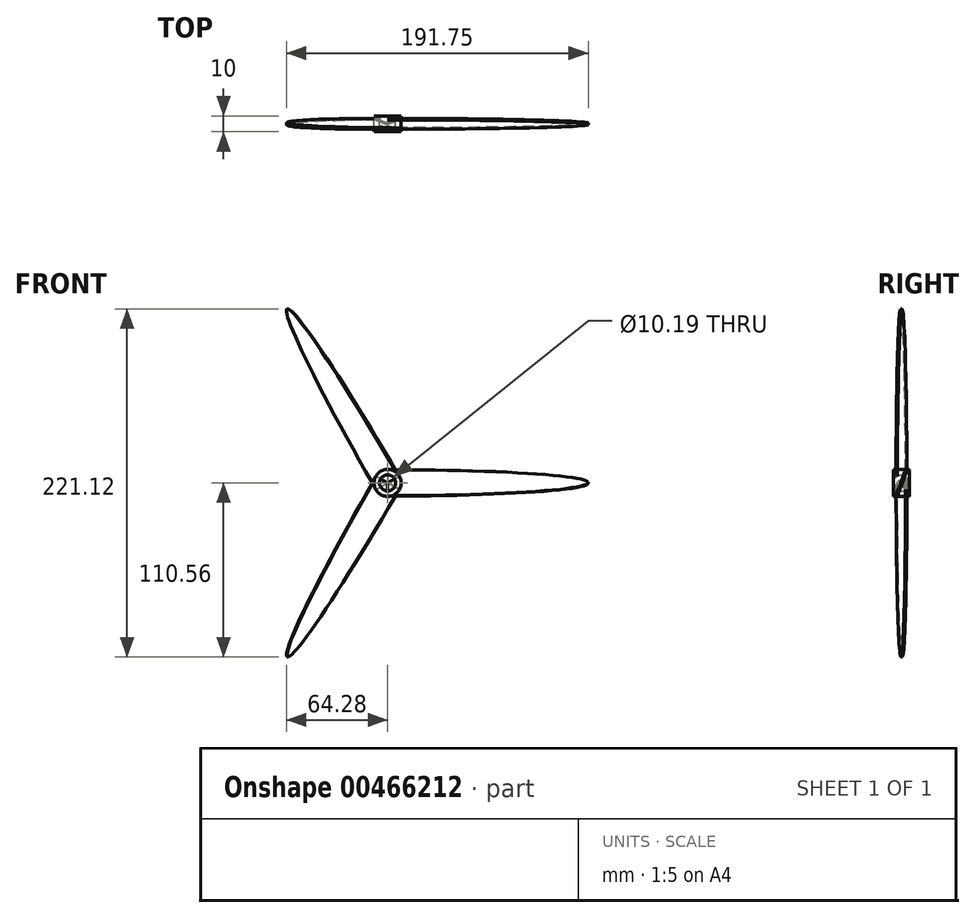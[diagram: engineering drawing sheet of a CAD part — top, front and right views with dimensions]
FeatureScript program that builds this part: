
annotation { "Feature Type Name" : "Feature", "Feature Type Description" : "" }
export const myFeature = defineFeature(function(context is Context, id is Id, definition is map)
    precondition{}
    {
        {
            var Q0;
            Q0=qCreatedBy(makeId("Front.planeOp"),FACE);
            var sketch = newSketch(context, id + "F0", { "sketchPlane" : qUnion([Q0])});
            skCircle(sketch, "E0", {"center": v(0, 0) * mm, "radius": 8.63 * mm});
            skCircle(sketch, "E1", {"center": v(0, 0) * mm, "radius": 5.1 * mm});
            skSolve(sketch);
        }
        {
            var Q0;
            Q0=qCreatedBy(makeId("Right.planeOp"),FACE);
            var sketch = newSketch(context, id + "F1", { "sketchPlane" : qUnion([Q0])});
            skLineSegment(sketch, "E2", {"start": v(23.78, 65.34) * mm, "end": v(-10.7, -29.37) * mm, "construction": true});
            skSolve(sketch);
        }
        {
            var Q0;
            Q0=qCreatedBy(makeId("Front.planeOp"),FACE);
            var Q1;
            Q1=sQuery(id+"F1.wireOp",EDGE,"E2");
            cPlane(context, id + "F2", {"entities" : qUnion([Q0, Q1]), "cplaneType" : CPlaneType.LINE_ANGLE, "offset" : 25 * mm, "angle" : 0 * degree, "width" : 150 * mm, "height" : 150 * mm});
        }
        {
            var Q0;
            Q0=qCreatedBy(id+"F2.planeOp",FACE);
            var sketch = newSketch(context, id + "F3", { "sketchPlane" : qUnion([Q0])});
            skEllipse(sketch, "E3", {"center": v(0, 0) * mm, "majorRadius": 127.47 * mm, "minorRadius": 8.77 * mm, "majorAxis": v(-1, 0)});
            skLineSegment(sketch, "E4", {"start": v(0, 8.77) * mm, "end": v(0, -8.77) * mm});
            skSolve(sketch);
        }
        {
            var Q0;
            {var subQ0=sQuery(id+"F3.wireOp",EDGE,"E4");Q0=makeQuery(id+"F3.imprint","IMPRINT",FACE,{"disambiguationData":[TD([[makeQuery(id+"F3.imprint","IMPRINT",EDGE,{"derivedFrom":subQ0}),-1.0]])]});}
            extrude(context, id + "F4", {"entities" : qUnion([Q0]), "endBound" : BoundingType.SYMMETRIC, "depth" : 1 * mm});
        }
        {
            var Q0;
            Q0=qCreatedBy(makeId("Top.planeOp"),FACE);
            var sketch = newSketch(context, id + "F5", { "sketchPlane" : qUnion([Q0])});
            skLineSegment(sketch, "E5", {"start": v(0, 41) * mm, "end": v(0, -39.52) * mm, "construction": true});
            skSolve(sketch);
        }
        {
            var Q0;
            Q0=makeQuery(id+"F4.opExtrude","SWEPT_BODY",BODY,{"disambiguationData":[OSD([sQuery(id+"F3.wireOp",EDGE,"E3"),sQuery(id+"F3.wireOp",EDGE,"E4")])]});
            var Q1;
            Q1=sQuery(id+"F5.wireOp",EDGE,"E5");
            circularPattern(context, id + "F6", {"entities" : qUnion([Q0]), "axis" : qUnion([Q1]), "angle" : 360 * degree, "instanceCount" : 3, "equalSpace" : true});
        }
        {
            var Q0;
            Q0=makeQuery(id+"F0.imprint","IMPRINT",FACE,{"disambiguationData":[TD([[makeQuery(id+"F0.imprint","IMPRINT",EDGE,{"derivedFrom":sQuery(id+"F0.wireOp",EDGE,"E0")}),1.0]])]});
            extrude(context, id + "F7", {"entities" : qUnion([Q0]), "endBound" : BoundingType.SYMMETRIC, "depth" : 10 * mm});
        }
    });
